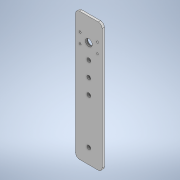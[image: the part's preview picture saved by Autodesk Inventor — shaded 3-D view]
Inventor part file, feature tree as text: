
AUTODESK INVENTOR PART (.ipt)
format: ipt  version: 2021 (Build 250183000, 183)  size: 117,760 bytes
history: native  units: mm
features: other x1, extrude x1, sketch x1
ambient origin geometry x8: Origin, YZ Plane, XZ Plane, XY Plane, X Axis, Y Axis, Z Axis, Center Point
bodies: Body1 (feature_tree)
feature tree (3):
  other  "Sólido1"
  extrude  "Extrusión1"  Depth=3.0mm
  sketch  "Boceto1"  dims[d23=3.0mm d24=0.0mm d25=0.5mm d26=0.872665mm]
